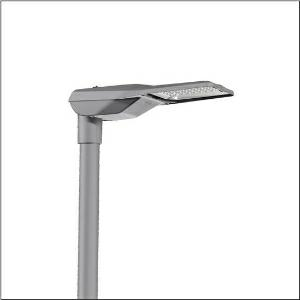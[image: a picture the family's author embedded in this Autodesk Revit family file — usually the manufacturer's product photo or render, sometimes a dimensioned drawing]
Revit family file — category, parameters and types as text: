
# Revit family: streetlight_sl_21_iq_mini___p0_8a_5xe2u31v08gb_4f31
name_source: partatom
category: Lighting Fixtures
units: mm (PartAtom-declared; Revit-internal decimal feet)

## family parameters
Cut with Voids When Loaded = No
Host = Face
Light Source = No
Part Type = Normal
Room Calculation Point = No
Round Connector Dimension = Use Diameter
Shared = No

## types (1)
- --- (1 x LED, 6040 lm, 39.8 W, 3000K)
    Apparent Load = 40 VA
    CIE Flux Codes = 33 69 96 100 100
    Color Rendering = 70
    Color Temperature = 3000K
    Default Elevation = 1800 mm
    Description = Streetlight SL 21 iQ mini, mast luminaire, primary light control with lens, of PMMA, primary optical cover: cover, of toughened safety glass, transparent, light distribution: P0.8a, light emission: direct distribution, primary light characteristic: asymmetric, installation type: post-top, side-entry, LED, High Power LED, rated luminous flux: 6.040lm, luminous efficacy: 152lm/W, light colour: 730, colour temperature: 3000K, control gear: iQ-Street Remote, D4i with power reduction, control: pre-setting: logarithmic dimming characteristic, Street-Remote, Auto-Match, Temp-Guard, Lumen-Switch, Night-Set, Smart-Wire, Light-Fading, Desk-Remote (wireless, voltage-free reading and setting of iQ features in the workshop via application-optimized NFC function/RFID function), optimised constant luminous flux control (CLO 2.0), mains connection: 220..240V, AC, 50/60Hz, start of lifetime: 40W, end of service life: 41W, reduction: 18W, luminaire housing, of diecast aluminium, powder-coated, Siteco® metallic grey (DB 702S), corrosivity category C5 mid according to DIN EN ISO 12944, please order mast flange separately, inclination adjustable: 0°, 5°, 10°, 15°, sealing non-destructively replaceable, multi-level sealing system, length: 628mm, width: 235mm, height: 110mm, mast flange for spigot size: 42mm (side-entry): 5XC10008XM4, 60/48mm (side-entry/post-top): 5XC10108XM2, 76/60mm (side-entry/post-top): 5XC10108XM1, mounting height: 4..8m, Smart Interface above, protection rating (complete): IP66, insulation class (complete): insulation class II (safety insulation), certification: CE, ENEC, ENEC+, VDE, impact resistance: IK10, permissible operating ambient temperature for outdoor applications: -40..+50°C, standard-compliant lighting for roads and squares, packaging unit: 1 piece

Light Distribution: P0.8a
    Height = 110 mm
    Lamp = 1 x LED
    Lamp Light Flux = 6040 lm
    Lamp Power = 39.8 W
    Lamp count = 1
    Length = 625 mm
    Luminous efficacy = 152 lm/W
    Manufacturer = Siteco
    ModVariant = No
    Model = 5XE2U31V08GB
    Number of Poles = 1
    OnlyDefault = Yes
    Power Factor = 1
    Product Name = Streetlight SL 21 iQ mini | P0.8a
    Product group = mast luminaire | pylon top
    ProductGroupID = 6100
    Protection Class = Protection class II
    Protection Degree = IP 66
    RLX_Detail_Level = 1
    RLX_Emergency_Light_Flux = 0 lm
    RLX_Emergency_Type = 0
    RLX_Emergency_Type_DB = No
    RlxData = <blob elided: 26373 chars, md5=2d1cc1e9>
    Socket = socket
    Standby Power = 0 W
    System Light Flux = 6040 lm
    System Power = 40 W
    Type Comments = factory setting: luminous flux: 100 % | dim-lin: 254 | 800 mA
    Type Image = l_1003515.jpg
    URL = http://relux.com
    VarID = @adj_074138
    Voltage = 0 V
    Weight = 0.00 kg
    Width = 234 mm

## geometry (parser evidence)
native form markers: Blend x4, Sweep x13
no freeform markers — native parametric forms only
